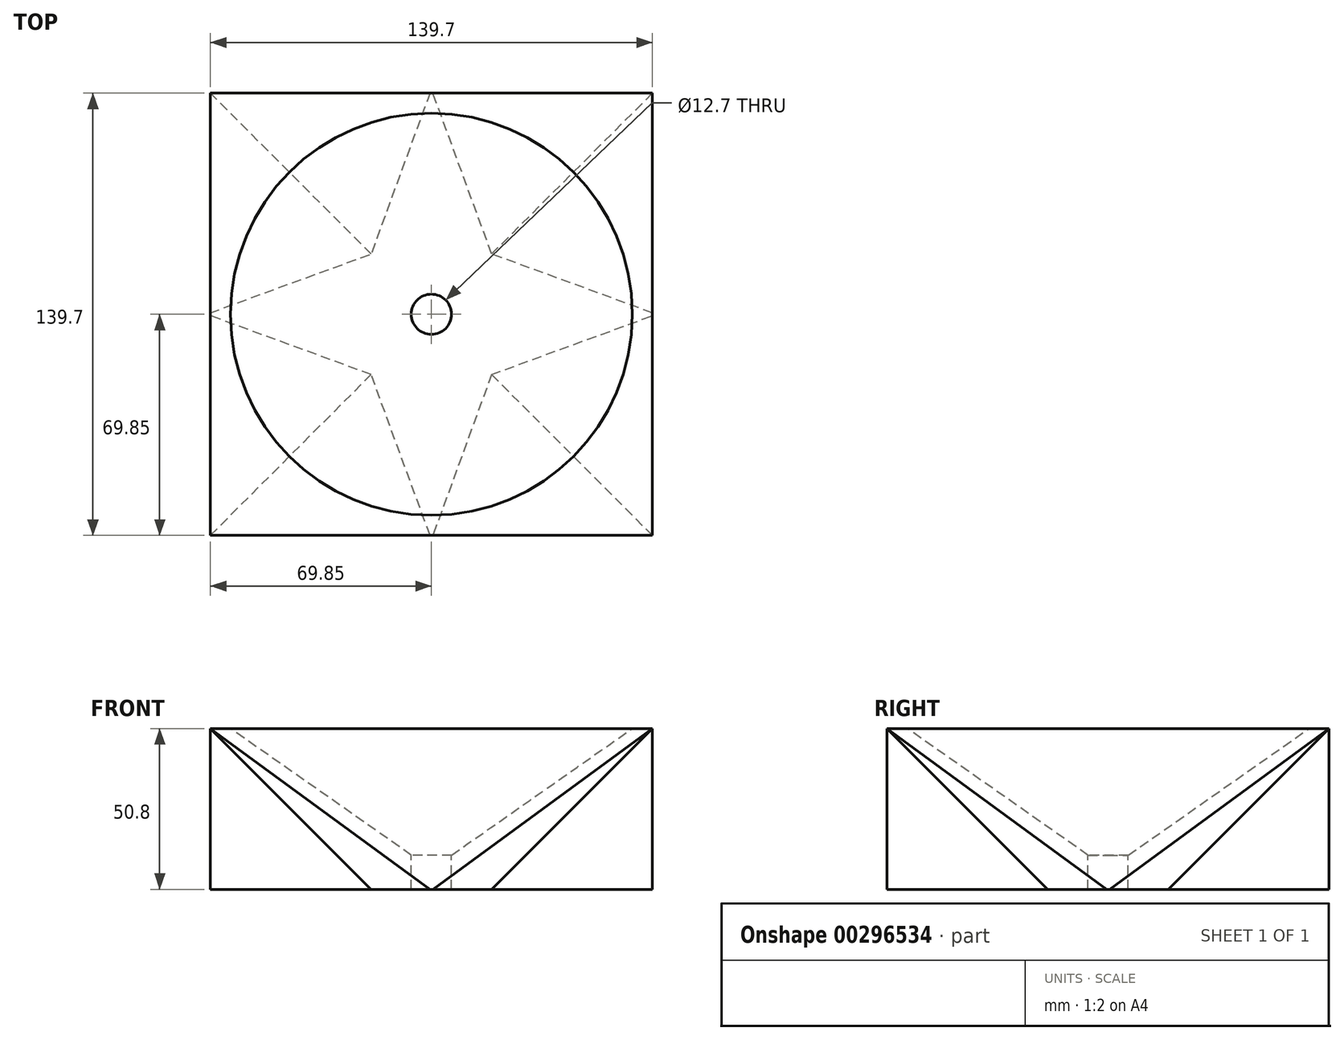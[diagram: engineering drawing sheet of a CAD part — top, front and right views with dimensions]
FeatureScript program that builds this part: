
annotation { "Feature Type Name" : "Feature", "Feature Type Description" : "" }
export const myFeature = defineFeature(function(context is Context, id is Id, definition is map)
    precondition{}
    {
        {
            var Q0;
            Q0=qCreatedBy(makeId("Top.planeOp"),FACE);
            var sketch = newSketch(context, id + "F0", { "sketchPlane" : qUnion([Q0])});
            skLineSegment(sketch, "E0.bottom", {"start": v(-38.1, 38.1) * mm, "end": v(0, 38.1) * mm});
            skLineSegment(sketch, "E0.top", {"start": v(-38.1, 0) * mm, "end": v(0, 0) * mm});
            skLineSegment(sketch, "E0.left", {"start": v(-38.1, 38.1) * mm, "end": v(-38.1, 0) * mm});
            skLineSegment(sketch, "E0.right", {"start": v(0, 38.1) * mm, "end": v(0, 0) * mm});
            skSolve(sketch);
        }
        {
            var Q0;
            Q0 = qSketchRegion(id + "F0", true);
            extrude(context, id + "F1", {"entities" : qUnion([Q0]), "depth" : 50.8 * mm, "hasDraft" : true, "draftAngle" : 45 * degree});
        }
        {
            var Q0;
            Q0=makeQuery(id+"F1.opExtrude","SWEPT_FACE",FACE,{"disambiguationData":[OSD([sQuery(id+"F0.wireOp",EDGE,"E0.top")])]});
            extrude(context, id + "F2", {"entities" : qUnion([Q0]), "operationType" : NewBodyOperationType.ADD, "depth" : 46.48 * mm, "hasDraft" : true, "draftAngle" : 45 * degree, "draftPullDirection" : true});
        }
        {
            var Q0;
            Q0=makeQuery(id+"F1.opExtrude","SWEPT_FACE",FACE,{"disambiguationData":[OSD([sQuery(id+"F0.wireOp",EDGE,"E0.right")])]});
            extrude(context, id + "F3", {"entities" : qUnion([Q0]), "operationType" : NewBodyOperationType.ADD, "depth" : 74.68 * mm, "hasDraft" : true, "draftAngle" : 45 * degree, "draftPullDirection" : true});
        }
        {
            var Q0;
            Q0=makeQuery(id+"F1.opExtrude","SWEPT_FACE",FACE,{"disambiguationData":[OSD([sQuery(id+"F0.wireOp",EDGE,"E0.left")])]});
            extrude(context, id + "F4", {"entities" : qUnion([Q0]), "operationType" : NewBodyOperationType.ADD, "depth" : 95 * mm, "hasDraft" : true, "draftAngle" : 45 * degree, "draftPullDirection" : true});
        }
        {
            var Q0;
            Q0=makeQuery(id+"F1.opExtrude","SWEPT_FACE",FACE,{"disambiguationData":[OSD([sQuery(id+"F0.wireOp",EDGE,"E0.bottom")])]});
            extrude(context, id + "F5", {"entities" : qUnion([Q0]), "operationType" : NewBodyOperationType.ADD, "depth" : 60.45 * mm, "hasDraft" : true, "draftAngle" : 45 * degree, "draftPullDirection" : true});
        }
        {
            var Q0;
            Q0=makeQuery(id+"F1.opExtrude","CAP_FACE",FACE,{"disambiguationData":[OSD([sQuery(id+"F0.wireOp",EDGE,"E0.bottom"),sQuery(id+"F0.wireOp",EDGE,"E0.top"),sQuery(id+"F0.wireOp",EDGE,"E0.left"),sQuery(id+"F0.wireOp",EDGE,"E0.right")])],"isStart":false});
            var sketch = newSketch(context, id + "F6", { "sketchPlane" : qUnion([Q0])});
            skPoint(sketch, "E1", {"position": v(-19.05, 19.05) * mm});
            skSolve(sketch);
        }
        {
            var Q0;
            Q0=sQuery(id+"F6.wireOp",VERTEX,"E1");
            var Q1;
            Q1=makeQuery(id+"F1.opExtrude","SWEPT_BODY",BODY,{"disambiguationData":[OSD([sQuery(id+"F0.wireOp",EDGE,"E0.bottom"),sQuery(id+"F0.wireOp",EDGE,"E0.top"),sQuery(id+"F0.wireOp",EDGE,"E0.left"),sQuery(id+"F0.wireOp",EDGE,"E0.right")])]});
            hole(context, id + "F7", {"style" : HoleStyle.C_SINK, "endStyle" : HoleEndStyle.THROUGH, "holeDiameter" : 12.7 * mm, "cSinkDiameter" : 127 * mm, "cSinkAngle" : 110 * degree, "tappedDepth" : 12.7 * mm, "tapClearance" : 3, "locations" : qUnion([Q0]), "scope" : qUnion([Q1])});
        }
    });
